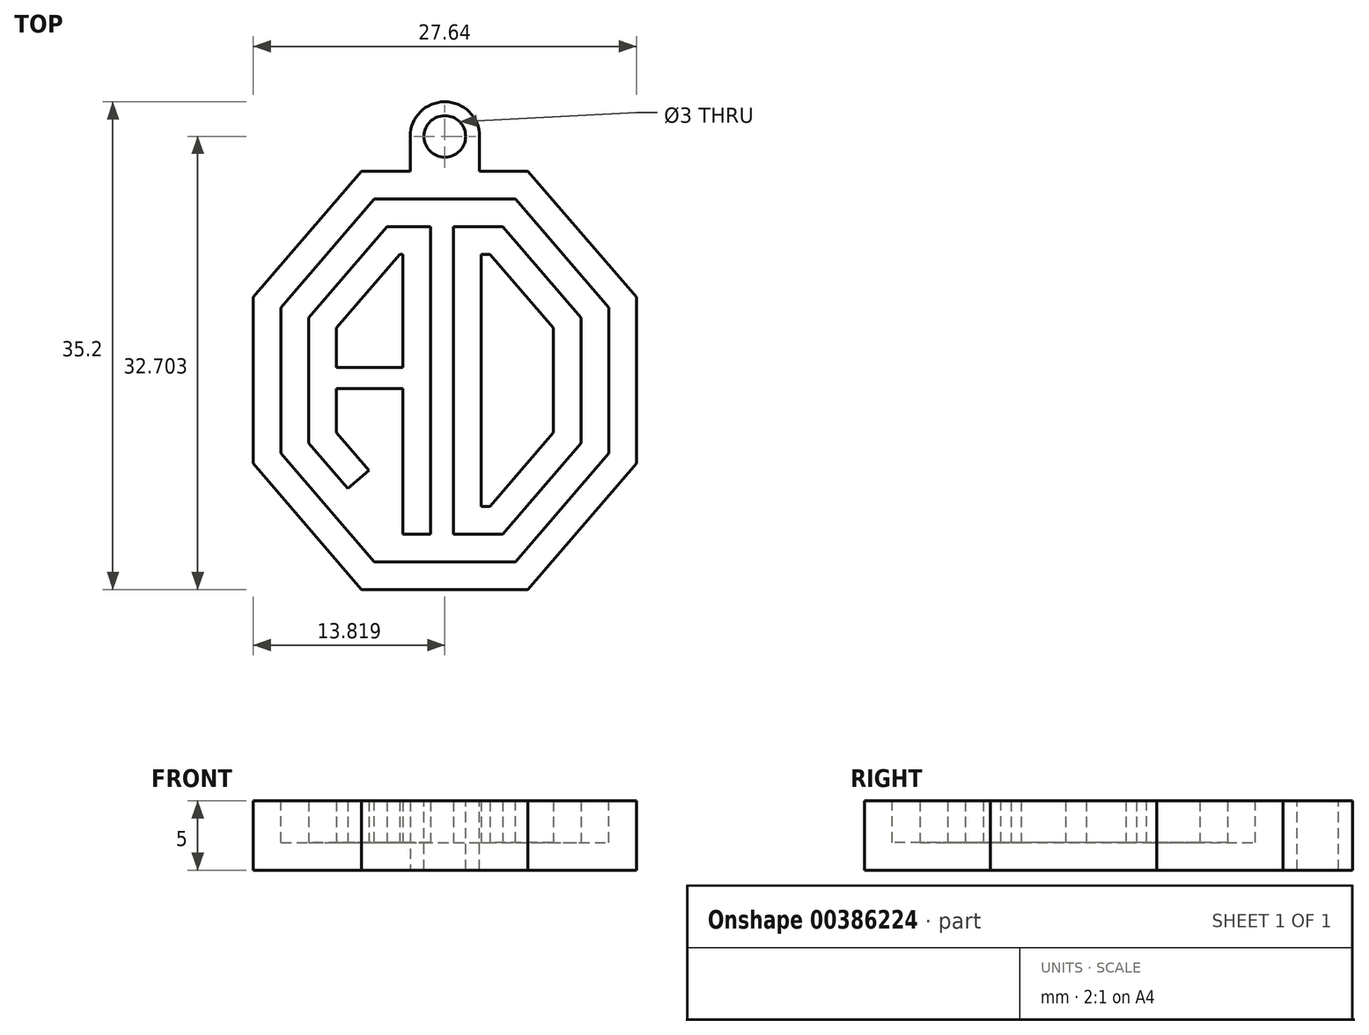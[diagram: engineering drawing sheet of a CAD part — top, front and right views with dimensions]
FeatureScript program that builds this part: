
annotation { "Feature Type Name" : "Feature", "Feature Type Description" : "" }
export const myFeature = defineFeature(function(context is Context, id is Id, definition is map)
    precondition{}
    {
        {
            var Q0;
            Q0=qCreatedBy(makeId("Top.planeOp"),FACE);
            var sketch = newSketch(context, id + "F0", { "sketchPlane" : qUnion([Q0])});
            skLineSegment(sketch, "E0", {"start": v(0, 0) * mm, "end": v(0, 6) * mm});
            skLineSegment(sketch, "E1", {"start": v(0, 0) * mm, "end": v(7.82, -9.1) * mm});
            skLineSegment(sketch, "E2", {"start": v(7.82, -9.1) * mm, "end": v(13.82, -9.1) * mm});
            skLineSegment(sketch, "E3.MirrorCS", {"start": v(0, 12) * mm, "end": v(0, 6) * mm});
            skLineSegment(sketch, "E4.MirrorCS", {"start": v(0, 12) * mm, "end": v(7.82, 21.1) * mm});
            skLineSegment(sketch, "E5.MirrorCS", {"start": v(7.82, 21.1) * mm, "end": v(13.82, 21.1) * mm});
            skLineSegment(sketch, "E6.MirrorCS", {"start": v(19.82, 21.1) * mm, "end": v(13.82, 21.1) * mm});
            skLineSegment(sketch, "E7.MirrorCS", {"start": v(27.64, 12) * mm, "end": v(19.82, 21.1) * mm});
            skLineSegment(sketch, "E8.MirrorCS", {"start": v(27.64, 12) * mm, "end": v(27.64, 6) * mm});
            skLineSegment(sketch, "E9.MirrorCS", {"start": v(27.64, 0) * mm, "end": v(27.64, 6) * mm});
            skLineSegment(sketch, "E10.MirrorCS", {"start": v(27.64, 0) * mm, "end": v(19.82, -9.1) * mm});
            skLineSegment(sketch, "E11.MirrorCS", {"start": v(19.82, -9.1) * mm, "end": v(13.82, -9.1) * mm});
            skSolve(sketch);
        }
        {
            var Q0;
            Q0 = qSketchRegion(id + "F0", true);
            extrude(context, id + "F1", {"entities" : qUnion([Q0]), "depth" : 5 * mm});
        }
        {
            var Q0;
            Q0=makeQuery(id+"F1.opExtrude","CAP_FACE",FACE,{"disambiguationData":[OSD([sQuery(id+"F0.wireOp",EDGE,"E0"),sQuery(id+"F0.wireOp",EDGE,"E1"),sQuery(id+"F0.wireOp",EDGE,"E2"),sQuery(id+"F0.wireOp",EDGE,"E3.MirrorCS"),sQuery(id+"F0.wireOp",EDGE,"E4.MirrorCS"),sQuery(id+"F0.wireOp",EDGE,"E5.MirrorCS"),sQuery(id+"F0.wireOp",EDGE,"E6.MirrorCS"),sQuery(id+"F0.wireOp",EDGE,"E7.MirrorCS"),sQuery(id+"F0.wireOp",EDGE,"E8.MirrorCS"),sQuery(id+"F0.wireOp",EDGE,"E9.MirrorCS"),sQuery(id+"F0.wireOp",EDGE,"E10.MirrorCS"),sQuery(id+"F0.wireOp",EDGE,"E11.MirrorCS")])],"isStart":false});
            var sketch = newSketch(context, id + "F2", { "sketchPlane" : qUnion([Q0])});
            skLineSegment(sketch, "E12.0", {"start": v(2, 0.74) * mm, "end": v(8.74, -7.1) * mm});
            skLineSegment(sketch, "E12.1", {"start": v(2, 11.26) * mm, "end": v(2, 0.74) * mm});
            skLineSegment(sketch, "E12.2", {"start": v(8.74, -7.1) * mm, "end": v(18.9, -7.1) * mm});
            skLineSegment(sketch, "E12.3", {"start": v(8.74, 19.1) * mm, "end": v(2, 11.26) * mm});
            skLineSegment(sketch, "E12.4", {"start": v(18.9, -7.1) * mm, "end": v(25.64, 0.74) * mm});
            skLineSegment(sketch, "E12.5", {"start": v(25.64, 0.74) * mm, "end": v(25.64, 11.26) * mm});
            skLineSegment(sketch, "E12.6", {"start": v(25.64, 11.26) * mm, "end": v(18.9, 19.1) * mm});
            skLineSegment(sketch, "E12.7", {"start": v(18.9, 19.1) * mm, "end": v(8.74, 19.1) * mm});
            skSolve(sketch);
        }
        {
            var Q0;
            Q0=makeQuery(id+"F2.imprint","IMPRINT",FACE,{"disambiguationData":[TD([[makeQuery(id+"F2.imprint","IMPRINT",EDGE,{"derivedFrom":sQuery(id+"F2.wireOp",EDGE,"E12.0")}),1.0]])]});
            extrude(context, id + "F3", {"entities" : qUnion([Q0]), "operationType" : NewBodyOperationType.REMOVE, "oppositeDirection" : true, "depth" : 3 * mm});
        }
        {
            var Q0;
            Q0=makeQuery(id+"F3.boolean.opBoolean","COPY",FACE,{"derivedFrom":makeQuery(id+"F3.opExtrude","CAP_FACE",FACE,{"disambiguationData":[OSD([sQuery(id+"F2.wireOp",EDGE,"E12.0"),sQuery(id+"F2.wireOp",EDGE,"E12.1"),sQuery(id+"F2.wireOp",EDGE,"E12.2"),sQuery(id+"F2.wireOp",EDGE,"E12.3"),sQuery(id+"F2.wireOp",EDGE,"E12.4"),sQuery(id+"F2.wireOp",EDGE,"E12.5"),sQuery(id+"F2.wireOp",EDGE,"E12.6"),sQuery(id+"F2.wireOp",EDGE,"E12.7")])],"isStart":false})});
            var sketch = newSketch(context, id + "F4", { "sketchPlane" : qUnion([Q0])});
            skLineSegment(sketch, "E13.0", {"start": v(23.64, 1.48) * mm, "end": v(23.64, 10.52) * mm});
            skLineSegment(sketch, "E13.1", {"start": v(17.98, -5.1) * mm, "end": v(23.64, 1.48) * mm});
            skLineSegment(sketch, "E13.2", {"start": v(23.64, 10.52) * mm, "end": v(17.98, 17.1) * mm});
            skLineSegment(sketch, "E13.3", {"start": v(10.79, -5.1) * mm, "end": v(12.79, -5.1) * mm});
            skLineSegment(sketch, "E13.4", {"start": v(17.98, 17.1) * mm, "end": v(14.44, 17.1) * mm});
            skLineSegment(sketch, "E13.5", {"start": v(9.66, 17.1) * mm, "end": v(4, 10.52) * mm});
            skLineSegment(sketch, "E13.6", {"start": v(4, 10.52) * mm, "end": v(4, 1.48) * mm});
            skLineSegment(sketch, "E13.7", {"start": v(4, 1.48) * mm, "end": v(6.83, -1.81) * mm});
            skLineSegment(sketch, "E14", {"start": v(12.79, 17.1) * mm, "end": v(12.79, -5.1) * mm});
            skLineSegment(sketch, "E15", {"start": v(14.44, 17.1) * mm, "end": v(14.44, -5.1) * mm});
            skLineSegment(sketch, "E16", {"start": v(6, 5.41) * mm, "end": v(10.79, 5.41) * mm});
            skLineSegment(sketch, "E17.0", {"start": v(16.44, 15.1) * mm, "end": v(16.44, -3.1) * mm});
            skLineSegment(sketch, "E18.0", {"start": v(30.64, -1.11) * mm, "end": v(30.64, 13.11) * mm});
            skLineSegment(sketch, "E18.1", {"start": v(21.2, -12.1) * mm, "end": v(30.64, -1.11) * mm});
            skLineSegment(sketch, "E18.2", {"start": v(30.64, 13.11) * mm, "end": v(21.2, 24.1) * mm});
            skLineSegment(sketch, "E18.3", {"start": v(6.44, -12.1) * mm, "end": v(21.2, -12.1) * mm});
            skLineSegment(sketch, "E18.4", {"start": v(21.2, 24.1) * mm, "end": v(6.44, 24.1) * mm});
            skLineSegment(sketch, "E18.5", {"start": v(6.44, 24.1) * mm, "end": v(-3, 13.11) * mm});
            skLineSegment(sketch, "E18.6", {"start": v(-3, 13.11) * mm, "end": v(-3, -1.11) * mm});
            skLineSegment(sketch, "E18.7", {"start": v(-3, -1.11) * mm, "end": v(6.44, -12.1) * mm});
            skLineSegment(sketch, "E19.0", {"start": v(21.64, 2.22) * mm, "end": v(21.64, 9.78) * mm});
            skLineSegment(sketch, "E19.1", {"start": v(17.06, -3.1) * mm, "end": v(21.64, 2.22) * mm});
            skLineSegment(sketch, "E19.2", {"start": v(21.64, 9.78) * mm, "end": v(17.06, 15.1) * mm});
            skLineSegment(sketch, "E19.3", {"start": v(10.58, -3.1) * mm, "end": v(10.79, -3.1) * mm});
            skLineSegment(sketch, "E19.4", {"start": v(17.06, 15.1) * mm, "end": v(16.44, 15.1) * mm});
            skLineSegment(sketch, "E19.5", {"start": v(10.58, 15.1) * mm, "end": v(6, 9.78) * mm});
            skLineSegment(sketch, "E19.6", {"start": v(6, 9.78) * mm, "end": v(6, 6.92) * mm});
            skLineSegment(sketch, "E19.7", {"start": v(6, 2.22) * mm, "end": v(8.35, -0.5) * mm});
            skLineSegment(sketch, "E20.trimOffspring", {"start": v(10.79, 15.1) * mm, "end": v(10.58, 15.1) * mm});
            skLineSegment(sketch, "E21.trimOffspring", {"start": v(12.79, 17.1) * mm, "end": v(9.66, 17.1) * mm});
            skLineSegment(sketch, "E22.trimOffspring", {"start": v(16.44, -3.1) * mm, "end": v(17.06, -3.1) * mm});
            skLineSegment(sketch, "E23.trimOffspring", {"start": v(14.44, -5.1) * mm, "end": v(17.98, -5.1) * mm});
            skLineSegment(sketch, "E24", {"start": v(6, 6.92) * mm, "end": v(10.79, 6.92) * mm});
            skLineSegment(sketch, "E25", {"start": v(10.79, 15.1) * mm, "end": v(10.79, 6.92) * mm});
            skLineSegment(sketch, "E26", {"start": v(6.83, -1.81) * mm, "end": v(8.35, -0.5) * mm});
            skPoint(sketch, "E27.orphan", {"position": v(9.66, -5.1) * mm});
            skLineSegment(sketch, "E28.trimOffspring", {"start": v(10.79, 5.41) * mm, "end": v(10.79, -5.1) * mm});
            skLineSegment(sketch, "E29.trimOffspring", {"start": v(6, 5.41) * mm, "end": v(6, 2.22) * mm});
            skSolve(sketch);
        }
        {
            var Q0;
            Q0=makeQuery(id+"F4.imprint","IMPRINT",FACE,{"disambiguationData":[TD([[makeQuery(id+"F4.imprint","IMPRINT",EDGE,{"derivedFrom":sQuery(id+"F4.wireOp",EDGE,"E13.0")}),1.0]])]});
            var Q1;
            {var subQ1=sQuery(id+"F4.wireOp",EDGE,"E13.3");Q1=makeQuery(id+"F4.imprint","IMPRINT",FACE,{"disambiguationData":[TD([[makeQuery(id+"F4.imprint","IMPRINT",EDGE,{"derivedFrom":subQ1}),1.0]])]});}
            extrude(context, id + "F5", {"entities" : qUnion([Q0, Q1]), "operationType" : NewBodyOperationType.ADD, "depth" : 3 * mm});
        }
        {
            var Q0;
            Q0=makeQuery(id+"F1.opExtrude","SWEPT_FACE",FACE,{"disambiguationData":[OSD([sQuery(id+"F0.wireOp",EDGE,"E5.MirrorCS"),sQuery(id+"F0.wireOp",EDGE,"E6.MirrorCS")])]});
            var sketch = newSketch(context, id + "F6", { "sketchPlane" : qUnion([Q0])});
            skLineSegment(sketch, "E30", {"start": v(-13.82, 5) * mm, "end": v(-16.32, 5) * mm});
            skLineSegment(sketch, "E31", {"start": v(-13.82, 5) * mm, "end": v(-11.32, 5) * mm});
            skLineSegment(sketch, "E32", {"start": v(-11.32, 5) * mm, "end": v(-11.32, 0) * mm});
            skLineSegment(sketch, "E33", {"start": v(-11.32, 0) * mm, "end": v(-16.32, 0) * mm});
            skLineSegment(sketch, "E34", {"start": v(-16.32, 0) * mm, "end": v(-16.32, 5) * mm});
            skPoint(sketch, "E35.orphan", {"position": v(-13.82, 2.5) * mm});
            skPoint(sketch, "E36.trimOffspring.end.orphan", {"position": v(-19.82, 2.5) * mm});
            skPoint(sketch, "E37.start.orphan", {"position": v(-7.82, 2.5) * mm});
            skSolve(sketch);
        }
        {
            var Q0;
            Q0 = qSketchRegion(id + "F6", true);
            extrude(context, id + "F7", {"entities" : qUnion([Q0]), "operationType" : NewBodyOperationType.ADD, "depth" : 5 * mm});
        }
        {
            var Q0;
            Q0=makeQuery(id+"F7.opExtrude","CAP_EDGE",EDGE,{"disambiguationData":[OSD([sQuery(id+"F6.wireOp",EDGE,"E32")])],"isStart":false});
            var Q1;
            Q1=makeQuery(id+"F7.opExtrude","CAP_EDGE",EDGE,{"disambiguationData":[OSD([sQuery(id+"F6.wireOp",EDGE,"E34")])],"isStart":false});
            fillet(context, id + "F8", {"entities" : qUnion([Q0, Q1]), "radius" : 2.5 * mm, "tangentPropagation" : true, "allowEdgeOverflow" : false});
        }
        {
            var Q0;
            Q0=makeQuery(id+"F7.boolean.opBoolean","MERGE",FACE,{"derivedFrom":[makeQuery(id+"F1.opExtrude","CAP_FACE",FACE,{"disambiguationData":[OSD([sQuery(id+"F0.wireOp",EDGE,"E0"),sQuery(id+"F0.wireOp",EDGE,"E1"),sQuery(id+"F0.wireOp",EDGE,"E2"),sQuery(id+"F0.wireOp",EDGE,"E3.MirrorCS"),sQuery(id+"F0.wireOp",EDGE,"E4.MirrorCS"),sQuery(id+"F0.wireOp",EDGE,"E5.MirrorCS"),sQuery(id+"F0.wireOp",EDGE,"E6.MirrorCS"),sQuery(id+"F0.wireOp",EDGE,"E7.MirrorCS"),sQuery(id+"F0.wireOp",EDGE,"E8.MirrorCS"),sQuery(id+"F0.wireOp",EDGE,"E9.MirrorCS"),sQuery(id+"F0.wireOp",EDGE,"E10.MirrorCS"),sQuery(id+"F0.wireOp",EDGE,"E11.MirrorCS")])],"isStart":false}),makeQuery(id+"F7.opExtrude","SWEPT_FACE",FACE,{"disambiguationData":[OSD([sQuery(id+"F6.wireOp",EDGE,"E30"),sQuery(id+"F6.wireOp",EDGE,"E31")])]})]});
            var sketch = newSketch(context, id + "F9", { "sketchPlane" : qUnion([Q0])});
            skCircle(sketch, "E38", {"center": v(13.82, 23.6) * mm, "radius": 1.5 * mm});
            skPoint(sketch, "E39.orphan", {"position": v(16.32, 23.6) * mm});
            skPoint(sketch, "E40.start.orphan", {"position": v(11.32, 23.6) * mm});
            skSolve(sketch);
        }
        {
            var Q0;
            Q0=makeQuery(id+"F9.imprint","IMPRINT",FACE,{"disambiguationData":[TD([[makeQuery(id+"F9.imprint","IMPRINT",EDGE,{"derivedFrom":sQuery(id+"F9.wireOp",EDGE,"E38")}),1.0]])]});
            extrude(context, id + "F10", {"entities" : qUnion([Q0]), "operationType" : NewBodyOperationType.REMOVE, "oppositeDirection" : true, "depth" : 5 * mm});
        }
    });
